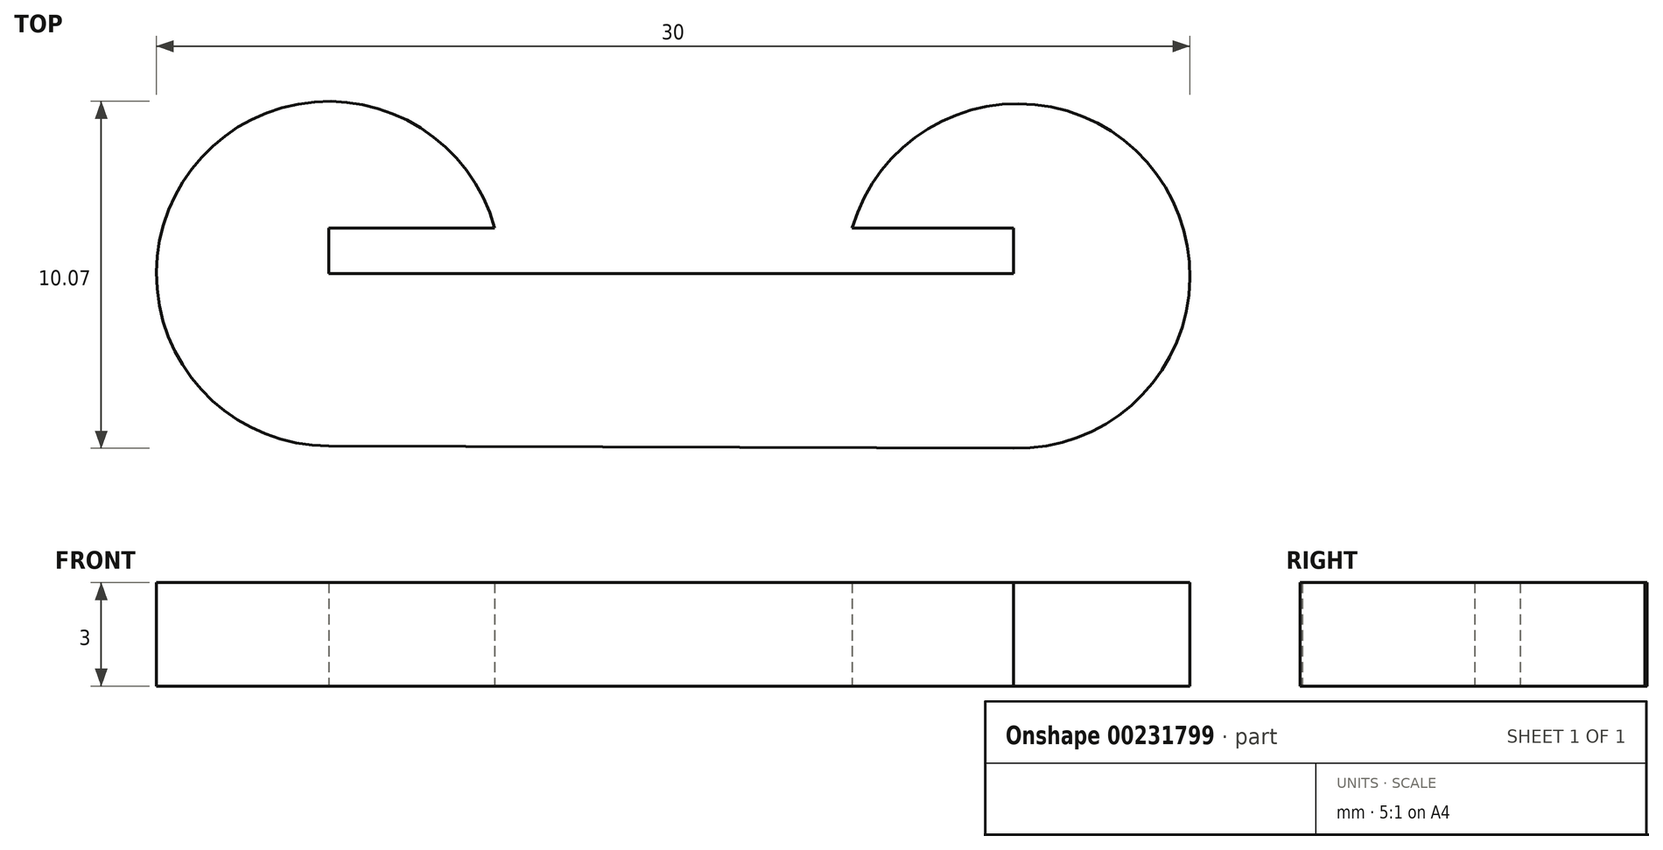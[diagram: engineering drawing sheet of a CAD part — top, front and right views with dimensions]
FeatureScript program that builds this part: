
annotation { "Feature Type Name" : "Feature", "Feature Type Description" : "" }
export const myFeature = defineFeature(function(context is Context, id is Id, definition is map)
    precondition{}
    {
        {
            var Q0;
            Q0=qCreatedBy(makeId("Top.planeOp"),FACE);
            var sketch = newSketch(context, id + "F0", { "sketchPlane" : qUnion([Q0])});
            skArc(sketch, "E0", {"start": v(0, -5.06) * mm, "mid": v(4.16, 2.89) * mm, "end": v(-4.68, 1.32) * mm});
            skArc(sketch, "E1", {"start": v(-15.05, 1.32) * mm, "mid": v(-23.85, 3.03) * mm, "end": v(-19.88, -5) * mm});
            skLineSegment(sketch, "E2", {"start": v(-19.88, -5) * mm, "end": v(0, -5.06) * mm});
            skLineSegment(sketch, "E3.bottom", {"start": v(-19.88, 0) * mm, "end": v(0, 0) * mm});
            skLineSegment(sketch, "E3.top", {"start": v(-19.88, 1.32) * mm, "end": v(-15.05, 1.32) * mm});
            skLineSegment(sketch, "E3.left", {"start": v(-19.88, 0) * mm, "end": v(-19.88, 1.32) * mm});
            skLineSegment(sketch, "E3.right", {"start": v(0, 0) * mm, "end": v(0, 1.32) * mm});
            skLineSegment(sketch, "E4.trimOffspring", {"start": v(-4.68, 1.32) * mm, "end": v(0, 1.32) * mm});
            skSolve(sketch);
        }
        {
            var Q0;
            Q0 = qSketchRegion(id + "F0", true);
            extrude(context, id + "F1", {"entities" : qUnion([Q0]), "depth" : 3 * mm});
        }
    });
